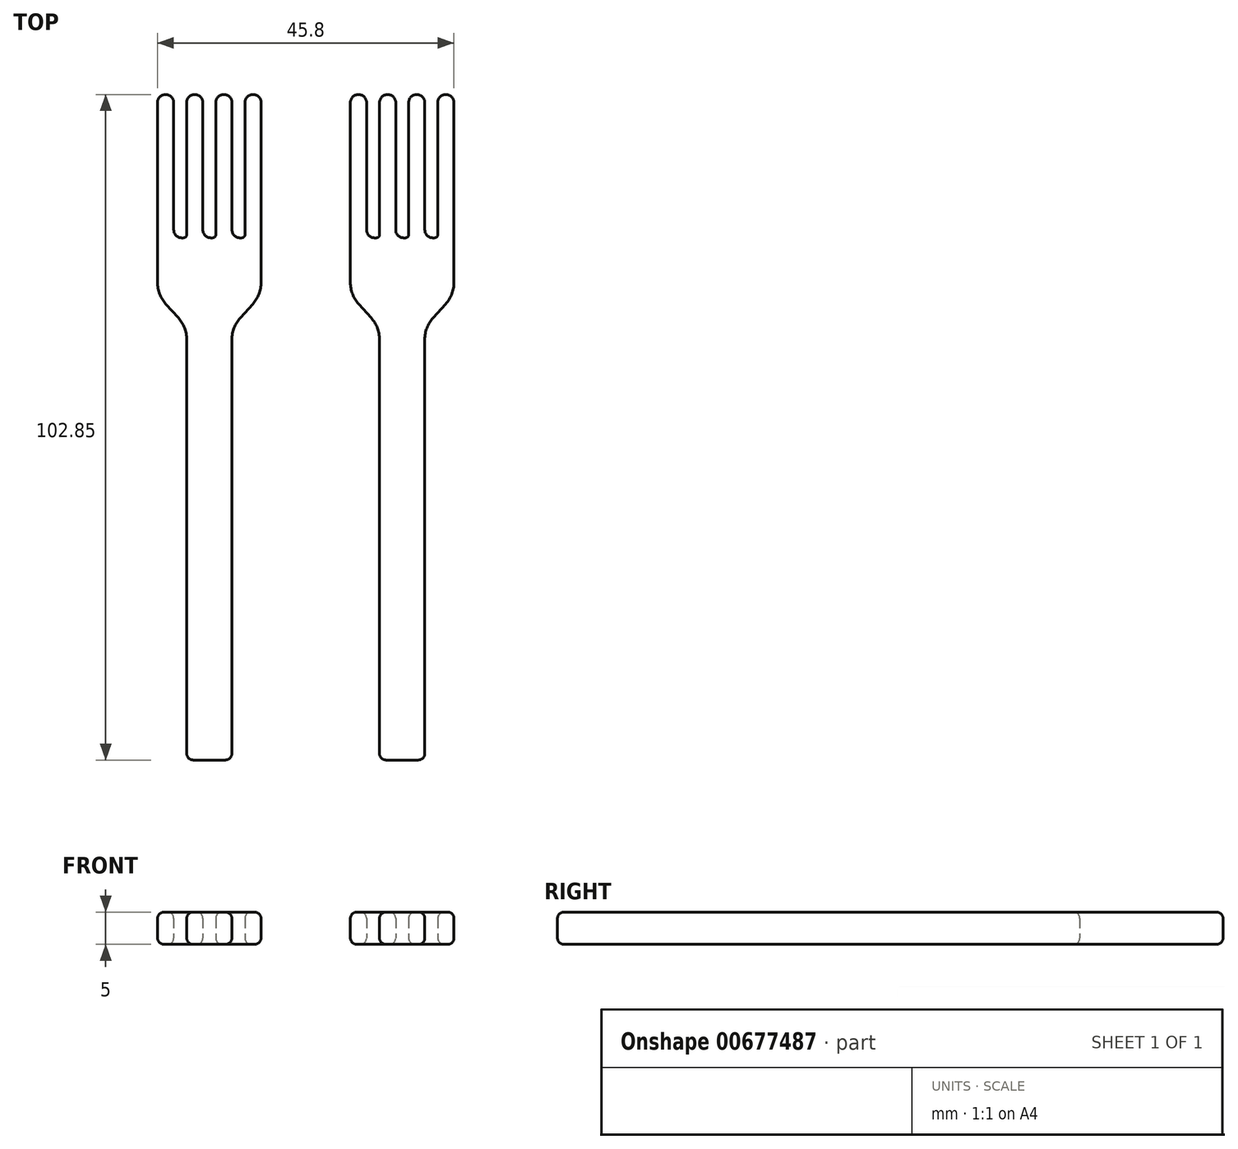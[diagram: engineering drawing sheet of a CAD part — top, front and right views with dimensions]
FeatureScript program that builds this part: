
annotation { "Feature Type Name" : "Feature", "Feature Type Description" : "" }
export const myFeature = defineFeature(function(context is Context, id is Id, definition is map)
    precondition{}
    {
        {
            var Q0;
            Q0=qCreatedBy(makeId("Top.planeOp"),FACE);
            var sketch = newSketch(context, id + "F0", { "sketchPlane" : qUnion([Q0])});
            skLineSegment(sketch, "E0", {"start": v(10.53, -44.06) * mm, "end": v(10.53, 20.94) * mm});
            skLineSegment(sketch, "E1", {"start": v(11.82, 24.3) * mm, "end": v(13.74, 26.41) * mm});
            skLineSegment(sketch, "E2", {"start": v(15.03, 29.77) * mm, "end": v(15.03, 57.57) * mm});
            skLineSegment(sketch, "E3", {"start": v(13.81, 58.79) * mm, "end": v(13.76, 58.79) * mm});
            skLineSegment(sketch, "E4", {"start": v(12.53, 57.57) * mm, "end": v(12.53, 37.13) * mm});
            skLineSegment(sketch, "E5", {"start": v(12.06, 36.65) * mm, "end": v(11.76, 36.65) * mm});
            skLineSegment(sketch, "E6", {"start": v(10.53, 37.87) * mm, "end": v(10.53, 57.57) * mm});
            skLineSegment(sketch, "E7", {"start": v(9.31, 58.79) * mm, "end": v(9.26, 58.79) * mm});
            skLineSegment(sketch, "E8", {"start": v(8.03, 57.57) * mm, "end": v(8.03, 37.13) * mm});
            skLineSegment(sketch, "E9", {"start": v(7.56, 36.65) * mm, "end": v(7.26, 36.65) * mm});
            skLineSegment(sketch, "E10", {"start": v(6.03, 37.87) * mm, "end": v(6.03, 57.57) * mm});
            skLineSegment(sketch, "E11", {"start": v(4.81, 58.79) * mm, "end": v(4.76, 58.79) * mm});
            skLineSegment(sketch, "E12", {"start": v(3.53, 57.57) * mm, "end": v(3.53, 37.13) * mm});
            skLineSegment(sketch, "E13", {"start": v(3.06, 36.65) * mm, "end": v(2.76, 36.65) * mm});
            skLineSegment(sketch, "E14", {"start": v(1.53, 37.87) * mm, "end": v(1.53, 57.57) * mm});
            skLineSegment(sketch, "E15", {"start": v(0.31, 58.79) * mm, "end": v(0.26, 58.79) * mm});
            skLineSegment(sketch, "E16", {"start": v(-0.97, 57.57) * mm, "end": v(-0.97, 36.65) * mm});
            skLineSegment(sketch, "E17", {"start": v(-0.97, 36.65) * mm, "end": v(-0.97, 29.77) * mm});
            skLineSegment(sketch, "E18", {"start": v(0.33, 26.41) * mm, "end": v(2.24, 24.3) * mm});
            skLineSegment(sketch, "E19", {"start": v(3.53, 20.94) * mm, "end": v(3.53, -44.06) * mm});
            skLineSegment(sketch, "E20", {"start": v(3.53, -44.06) * mm, "end": v(10.53, -44.06) * mm});
            skPoint(sketch, "E21.visualSharp", {"position": v(-0.97, 27.84) * mm});
            skArc(sketch, "E21.filletArc", {"start": v(-0.97, 29.77) * mm, "mid": v(-0.63, 27.97) * mm, "end": v(0.33, 26.41) * mm});
            skPoint(sketch, "E22.visualSharp", {"position": v(15.03, 27.84) * mm});
            skArc(sketch, "E22.filletArc", {"start": v(13.74, 26.41) * mm, "mid": v(14.7, 27.97) * mm, "end": v(15.03, 29.77) * mm});
            skPoint(sketch, "E23.visualSharp", {"position": v(3.53, 22.87) * mm});
            skArc(sketch, "E23.filletArc", {"start": v(3.53, 20.94) * mm, "mid": v(3.2, 22.74) * mm, "end": v(2.24, 24.3) * mm});
            skPoint(sketch, "E24.visualSharp", {"position": v(10.53, 22.87) * mm});
            skArc(sketch, "E24.filletArc", {"start": v(11.82, 24.3) * mm, "mid": v(10.86, 22.74) * mm, "end": v(10.53, 20.94) * mm});
            skPoint(sketch, "E25.visualSharp", {"position": v(3.53, 58.79) * mm});
            skArc(sketch, "E25.filletArc", {"start": v(4.76, 58.79) * mm, "mid": v(3.9, 58.43) * mm, "end": v(3.53, 57.57) * mm});
            skPoint(sketch, "E26.visualSharp", {"position": v(6.03, 58.79) * mm});
            skArc(sketch, "E26.filletArc", {"start": v(6.03, 57.57) * mm, "mid": v(5.68, 58.43) * mm, "end": v(4.81, 58.79) * mm});
            skPoint(sketch, "E27.visualSharp", {"position": v(8.03, 58.79) * mm});
            skArc(sketch, "E27.filletArc", {"start": v(9.26, 58.79) * mm, "mid": v(8.4, 58.43) * mm, "end": v(8.03, 57.57) * mm});
            skPoint(sketch, "E28.visualSharp", {"position": v(10.53, 58.79) * mm});
            skArc(sketch, "E28.filletArc", {"start": v(10.53, 57.57) * mm, "mid": v(10.18, 58.43) * mm, "end": v(9.31, 58.79) * mm});
            skPoint(sketch, "E29.visualSharp", {"position": v(12.53, 58.79) * mm});
            skArc(sketch, "E29.filletArc", {"start": v(13.76, 58.79) * mm, "mid": v(12.9, 58.43) * mm, "end": v(12.53, 57.57) * mm});
            skPoint(sketch, "E30.visualSharp", {"position": v(15.03, 58.79) * mm});
            skArc(sketch, "E30.filletArc", {"start": v(15.03, 57.57) * mm, "mid": v(14.68, 58.43) * mm, "end": v(13.81, 58.79) * mm});
            skPoint(sketch, "E31.visualSharp", {"position": v(-0.97, 58.79) * mm});
            skArc(sketch, "E31.filletArc", {"start": v(0.26, 58.79) * mm, "mid": v(-0.6, 58.43) * mm, "end": v(-0.97, 57.57) * mm});
            skPoint(sketch, "E32.visualSharp", {"position": v(1.53, 58.79) * mm});
            skArc(sketch, "E32.filletArc", {"start": v(1.53, 57.57) * mm, "mid": v(1.18, 58.43) * mm, "end": v(0.31, 58.79) * mm});
            skPoint(sketch, "E33.visualSharp", {"position": v(1.53, 36.65) * mm});
            skArc(sketch, "E33.filletArc", {"start": v(1.53, 37.87) * mm, "mid": v(1.9, 37) * mm, "end": v(2.76, 36.65) * mm});
            skPoint(sketch, "E34.visualSharp", {"position": v(6.03, 36.65) * mm});
            skArc(sketch, "E34.filletArc", {"start": v(6.03, 37.87) * mm, "mid": v(6.4, 37) * mm, "end": v(7.26, 36.65) * mm});
            skPoint(sketch, "E35.visualSharp", {"position": v(10.53, 36.65) * mm});
            skArc(sketch, "E35.filletArc", {"start": v(10.53, 37.87) * mm, "mid": v(10.9, 37) * mm, "end": v(11.76, 36.65) * mm});
            skPoint(sketch, "E36.visualSharp", {"position": v(3.53, 36.65) * mm});
            skArc(sketch, "E36.filletArc", {"start": v(3.06, 36.65) * mm, "mid": v(3.4, 36.79) * mm, "end": v(3.53, 37.13) * mm});
            skPoint(sketch, "E37.visualSharp", {"position": v(8.03, 36.65) * mm});
            skArc(sketch, "E37.filletArc", {"start": v(7.56, 36.65) * mm, "mid": v(7.9, 36.79) * mm, "end": v(8.03, 37.13) * mm});
            skPoint(sketch, "E38.visualSharp", {"position": v(12.53, 36.65) * mm});
            skArc(sketch, "E38.filletArc", {"start": v(12.06, 36.65) * mm, "mid": v(12.4, 36.79) * mm, "end": v(12.53, 37.13) * mm});
            skSolve(sketch);
        }
        {
            var Q0;
            Q0=makeQuery(id+"F0.imprint","IMPRINT",FACE,{"disambiguationData":[TD([[makeQuery(id+"F0.imprint","IMPRINT",EDGE,{"derivedFrom":sQuery(id+"F0.wireOp",EDGE,"E0")}),1.0]])]});
            extrude(context, id + "F1", {"entities" : qUnion([Q0]), "depth" : 5 * mm, "offsetDistance" : 25 * mm});
        }
        {
            var Q0;
            Q0=makeQuery(id+"F1.opExtrude","CAP_FACE",FACE,{"disambiguationData":[OSD([sQuery(id+"F0.wireOp",EDGE,"E0"),sQuery(id+"F0.wireOp",EDGE,"E1"),sQuery(id+"F0.wireOp",EDGE,"E2"),sQuery(id+"F0.wireOp",EDGE,"E3"),sQuery(id+"F0.wireOp",EDGE,"E4"),sQuery(id+"F0.wireOp",EDGE,"E5"),sQuery(id+"F0.wireOp",EDGE,"E6"),sQuery(id+"F0.wireOp",EDGE,"E7"),sQuery(id+"F0.wireOp",EDGE,"E8"),sQuery(id+"F0.wireOp",EDGE,"E9"),sQuery(id+"F0.wireOp",EDGE,"E10"),sQuery(id+"F0.wireOp",EDGE,"E11"),sQuery(id+"F0.wireOp",EDGE,"E12"),sQuery(id+"F0.wireOp",EDGE,"E13"),sQuery(id+"F0.wireOp",EDGE,"E14"),sQuery(id+"F0.wireOp",EDGE,"E15"),sQuery(id+"F0.wireOp",EDGE,"E16"),sQuery(id+"F0.wireOp",EDGE,"E17"),sQuery(id+"F0.wireOp",EDGE,"E18"),sQuery(id+"F0.wireOp",EDGE,"E19"),sQuery(id+"F0.wireOp",EDGE,"E20"),sQuery(id+"F0.wireOp",EDGE,"E21.filletArc"),sQuery(id+"F0.wireOp",EDGE,"E22.filletArc"),sQuery(id+"F0.wireOp",EDGE,"E23.filletArc"),sQuery(id+"F0.wireOp",EDGE,"E24.filletArc"),sQuery(id+"F0.wireOp",EDGE,"E25.filletArc"),sQuery(id+"F0.wireOp",EDGE,"E26.filletArc"),sQuery(id+"F0.wireOp",EDGE,"E27.filletArc"),sQuery(id+"F0.wireOp",EDGE,"E28.filletArc"),sQuery(id+"F0.wireOp",EDGE,"E29.filletArc"),sQuery(id+"F0.wireOp",EDGE,"E30.filletArc"),sQuery(id+"F0.wireOp",EDGE,"E31.filletArc"),sQuery(id+"F0.wireOp",EDGE,"E32.filletArc"),sQuery(id+"F0.wireOp",EDGE,"E33.filletArc"),sQuery(id+"F0.wireOp",EDGE,"E34.filletArc"),sQuery(id+"F0.wireOp",EDGE,"E35.filletArc"),sQuery(id+"F0.wireOp",EDGE,"E36.filletArc"),sQuery(id+"F0.wireOp",EDGE,"E37.filletArc"),sQuery(id+"F0.wireOp",EDGE,"E38.filletArc")])],"isStart":false});
            var Q1;
            Q1=makeQuery(id+"F1.opExtrude","CAP_FACE",FACE,{"disambiguationData":[OSD([sQuery(id+"F0.wireOp",EDGE,"E0"),sQuery(id+"F0.wireOp",EDGE,"E1"),sQuery(id+"F0.wireOp",EDGE,"E2"),sQuery(id+"F0.wireOp",EDGE,"E3"),sQuery(id+"F0.wireOp",EDGE,"E4"),sQuery(id+"F0.wireOp",EDGE,"E5"),sQuery(id+"F0.wireOp",EDGE,"E6"),sQuery(id+"F0.wireOp",EDGE,"E7"),sQuery(id+"F0.wireOp",EDGE,"E8"),sQuery(id+"F0.wireOp",EDGE,"E9"),sQuery(id+"F0.wireOp",EDGE,"E10"),sQuery(id+"F0.wireOp",EDGE,"E11"),sQuery(id+"F0.wireOp",EDGE,"E12"),sQuery(id+"F0.wireOp",EDGE,"E13"),sQuery(id+"F0.wireOp",EDGE,"E14"),sQuery(id+"F0.wireOp",EDGE,"E15"),sQuery(id+"F0.wireOp",EDGE,"E16"),sQuery(id+"F0.wireOp",EDGE,"E17"),sQuery(id+"F0.wireOp",EDGE,"E18"),sQuery(id+"F0.wireOp",EDGE,"E19"),sQuery(id+"F0.wireOp",EDGE,"E20"),sQuery(id+"F0.wireOp",EDGE,"E21.filletArc"),sQuery(id+"F0.wireOp",EDGE,"E22.filletArc"),sQuery(id+"F0.wireOp",EDGE,"E23.filletArc"),sQuery(id+"F0.wireOp",EDGE,"E24.filletArc"),sQuery(id+"F0.wireOp",EDGE,"E25.filletArc"),sQuery(id+"F0.wireOp",EDGE,"E26.filletArc"),sQuery(id+"F0.wireOp",EDGE,"E27.filletArc"),sQuery(id+"F0.wireOp",EDGE,"E28.filletArc"),sQuery(id+"F0.wireOp",EDGE,"E29.filletArc"),sQuery(id+"F0.wireOp",EDGE,"E30.filletArc"),sQuery(id+"F0.wireOp",EDGE,"E31.filletArc"),sQuery(id+"F0.wireOp",EDGE,"E32.filletArc"),sQuery(id+"F0.wireOp",EDGE,"E33.filletArc"),sQuery(id+"F0.wireOp",EDGE,"E34.filletArc"),sQuery(id+"F0.wireOp",EDGE,"E35.filletArc"),sQuery(id+"F0.wireOp",EDGE,"E36.filletArc"),sQuery(id+"F0.wireOp",EDGE,"E37.filletArc"),sQuery(id+"F0.wireOp",EDGE,"E38.filletArc")])],"isStart":true});
            var Q2;
            Q2=makeQuery(id+"F1.opExtrude","SWEPT_FACE",FACE,{"disambiguationData":[OSD([sQuery(id+"F0.wireOp",EDGE,"E30.filletArc")])]});
            var Q3;
            Q3=makeQuery(id+"F1.opExtrude","CAP_EDGE",EDGE,{"disambiguationData":[OSD([sQuery(id+"F0.wireOp",EDGE,"E19")])],"isStart":true});
            var Q4;
            Q4=makeQuery(id+"F1.opExtrude","SWEPT_FACE",FACE,{"disambiguationData":[OSD([sQuery(id+"F0.wireOp",EDGE,"E0")])]});
            var Q5;
            Q5=makeQuery(id+"F1.opExtrude","SWEPT_EDGE",EDGE,{"disambiguationData":[OSD([sQuery(id+"F0.wireOp",EDGE,"E19"),sQuery(id+"F0.wireOp",EDGE,"E20")])]});
            fillet(context, id + "F2", {"entities" : qUnion([Q0, Q1, Q2, Q3, Q4, Q5]), "radius" : 1 * mm, "tangentPropagation" : true, "allowEdgeOverflow" : false});
        }
        {
            var Q0;
            Q0=makeQuery(id+"F1.opExtrude","SWEPT_BODY",BODY,{"disambiguationData":[OSD([sQuery(id+"F0.wireOp",EDGE,"E0"),sQuery(id+"F0.wireOp",EDGE,"E1"),sQuery(id+"F0.wireOp",EDGE,"E2"),sQuery(id+"F0.wireOp",EDGE,"E3"),sQuery(id+"F0.wireOp",EDGE,"E4"),sQuery(id+"F0.wireOp",EDGE,"E5"),sQuery(id+"F0.wireOp",EDGE,"E6"),sQuery(id+"F0.wireOp",EDGE,"E7"),sQuery(id+"F0.wireOp",EDGE,"E8"),sQuery(id+"F0.wireOp",EDGE,"E9"),sQuery(id+"F0.wireOp",EDGE,"E10"),sQuery(id+"F0.wireOp",EDGE,"E11"),sQuery(id+"F0.wireOp",EDGE,"E12"),sQuery(id+"F0.wireOp",EDGE,"E13"),sQuery(id+"F0.wireOp",EDGE,"E14"),sQuery(id+"F0.wireOp",EDGE,"E15"),sQuery(id+"F0.wireOp",EDGE,"E16"),sQuery(id+"F0.wireOp",EDGE,"E17"),sQuery(id+"F0.wireOp",EDGE,"E18"),sQuery(id+"F0.wireOp",EDGE,"E19"),sQuery(id+"F0.wireOp",EDGE,"E20"),sQuery(id+"F0.wireOp",EDGE,"E21.filletArc"),sQuery(id+"F0.wireOp",EDGE,"E22.filletArc"),sQuery(id+"F0.wireOp",EDGE,"E23.filletArc"),sQuery(id+"F0.wireOp",EDGE,"E24.filletArc"),sQuery(id+"F0.wireOp",EDGE,"E25.filletArc"),sQuery(id+"F0.wireOp",EDGE,"E26.filletArc"),sQuery(id+"F0.wireOp",EDGE,"E27.filletArc"),sQuery(id+"F0.wireOp",EDGE,"E28.filletArc"),sQuery(id+"F0.wireOp",EDGE,"E29.filletArc"),sQuery(id+"F0.wireOp",EDGE,"E30.filletArc"),sQuery(id+"F0.wireOp",EDGE,"E31.filletArc"),sQuery(id+"F0.wireOp",EDGE,"E32.filletArc"),sQuery(id+"F0.wireOp",EDGE,"E33.filletArc"),sQuery(id+"F0.wireOp",EDGE,"E34.filletArc"),sQuery(id+"F0.wireOp",EDGE,"E35.filletArc"),sQuery(id+"F0.wireOp",EDGE,"E36.filletArc"),sQuery(id+"F0.wireOp",EDGE,"E37.filletArc"),sQuery(id+"F0.wireOp",EDGE,"E38.filletArc")])]});
            transform(context, id + "F3", {"entities" : qUnion([Q0]), "transformType" : TransformType.TRANSLATION_3D, "dx" : 29.8 * mm, "dy" : 0 * mm, "dz" : 0 * mm, "makeCopy" : true});
        }
    });
